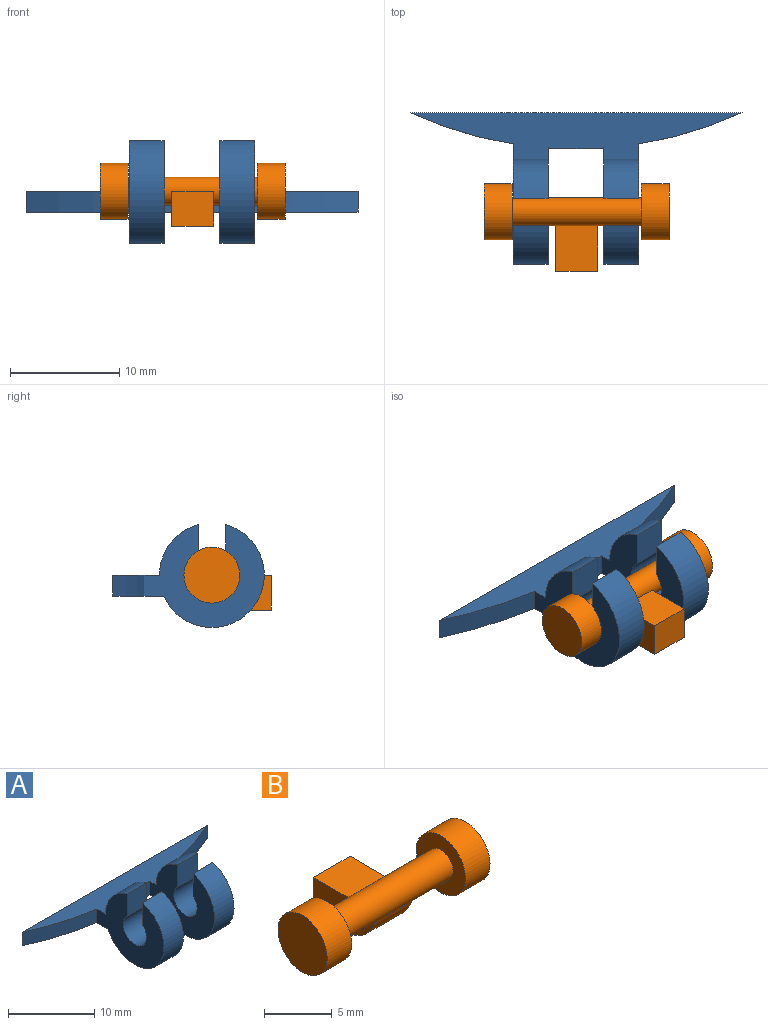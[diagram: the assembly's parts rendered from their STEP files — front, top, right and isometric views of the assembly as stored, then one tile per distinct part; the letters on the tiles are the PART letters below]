
ASSEMBLY  parts=2 mates=1
PART A: 20 faces, bbox 30.4x13.9x9.4 mm
  f0: plane 30.42x4.28mm, normal (0,0,1), area 75.7mm2, adj f1,f2,f3,f4,f5,f7,f8,f9
  f1: cylinder r=36.48mm len=9.45mm, axis (0,0,1), area 19mm2, adj f0,f6,f9,f19
  f2: cylinder r=4.8mm len=4.64mm, axis (1,0,0), area 20.1mm2, adj f0,f9,f10,f17
  f3: cylinder r=4.8mm len=4.64mm, axis (-1,0,0), area 20.1mm2, adj f0,f4,f5,f15
  f4: plane 11.02x9.44mm, normal (-1,0,0), area 56.3mm2, adj f0,f3,f6,f8,f13,f14,f15,f16
  f5: plane 10.65x9.44mm, normal (1,0,0), area 55.6mm2, adj f0,f3,f6,f7,f13,f14,f15,f16
  f6: plane 30.42x4.68mm, normal (0,0,-1), area 78.3mm2, adj f1,f4,f5,f7,f8,f9,f10,f12
  f7: cylinder r=36.48mm len=5.12mm, axis (0,0,1), area 9.8mm2, adj f0,f5,f6,f10
  f8: cylinder r=36.48mm len=9.45mm, axis (0,0,1), area 19mm2, adj f0,f4,f6,f19
  f9: plane 11.02x9.44mm, normal (1,0,0), area 56.3mm2, adj f0,f1,f2,f6,f11,f12,f17,f18
  f10: plane 10.65x9.44mm, normal (-1,0,0), area 55.6mm2, adj f0,f2,f6,f7,f11,f12,f17,f18
  f11: cylinder r=1.92mm len=3.84mm, axis (1,0,0), area 29.9mm2, adj f9,f10,f17,f18
  f12: cylinder r=4.8mm len=9.43mm, axis (1,0,0), area 62mm2, adj f6,f9,f10,f18
  f13: cylinder r=1.92mm len=3.84mm, axis (-1,0,0), area 29.9mm2, adj f4,f5,f15,f16
  f14: cylinder r=4.8mm len=9.43mm, axis (-1,0,0), area 62mm2, adj f4,f5,f6,f16
  f15: plane 3.2x3.17mm, normal (0,-1,0), area 10.1mm2, adj f3,f4,f5,f13
  f16: plane 3.2x3.18mm, normal (0,1,0), area 10.2mm2, adj f4,f5,f13,f14
  f17: plane 3.2x3.17mm, normal (0,-1,0), area 10.1mm2, adj f2,f9,f10,f11
  f18: plane 3.2x3.18mm, normal (0,1,0), area 10.2mm2, adj f9,f10,f11,f12
  f19: plane 30.42x1.92mm, normal (0,1,0), area 58.4mm2, adj f0,f1,f6,f8
PART B: 13 faces, bbox 17x8x5.8 mm
  f0: plane 4.16x3.84mm, normal (0,0,1), area 16mm2, adj f1,f2,f3,f12
  f1: plane 6.4x3.2mm, normal (1,0,0), area 16.2mm2, adj f0,f3,f10,f11,f12
  f2: plane 6.4x3.2mm, normal (-1,0,0), area 16.2mm2, adj f0,f3,f10,f11,f12
  f3: cylinder r=1.28mm len=11.84mm, axis (-1,0,0), area 83.3mm2, adj f0,f1,f2,f6,f9,f11
  f4: cylinder r=2.56mm len=5.12mm, axis (-1,0,0), area 41.2mm2, adj f5,f6
  f5: plane 5.12x5.12mm, normal (1,0,0), area 20.6mm2, adj f4
  f6: plane 5.12x5.12mm, normal (-1,0,0), area 15.4mm2, adj f3,f4
  f7: cylinder r=2.56mm len=5.12mm, axis (1,0,0), area 41.2mm2, adj f8,f9
  f8: plane 5.12x5.12mm, normal (-1,0,0), area 20.6mm2, adj f7
  f9: plane 5.12x5.12mm, normal (1,0,0), area 15.4mm2, adj f3,f7
  f10: plane 3.84x3.32mm, normal (0,0,-1), area 12.7mm2, adj f1,f2,f11,f12
  f11: cylinder r=3.2mm len=3.84mm, axis (-1,0,0), area 16mm2, adj f1,f2,f3,f10
  f12: plane 3.84x3.2mm, normal (0,1,0), area 12.3mm2, adj f0,f1,f2,f10
PLACE A t=(-7.95,2.97,0.15)mm
PLACE B rot(axis=(0,0,1),180deg) t=(-7.89,-81.51,0.15)mm
MATE revolute B.f3 <-> A.f2  axis (1,0,0) through (-7.89,-39.27,0.15)mm
